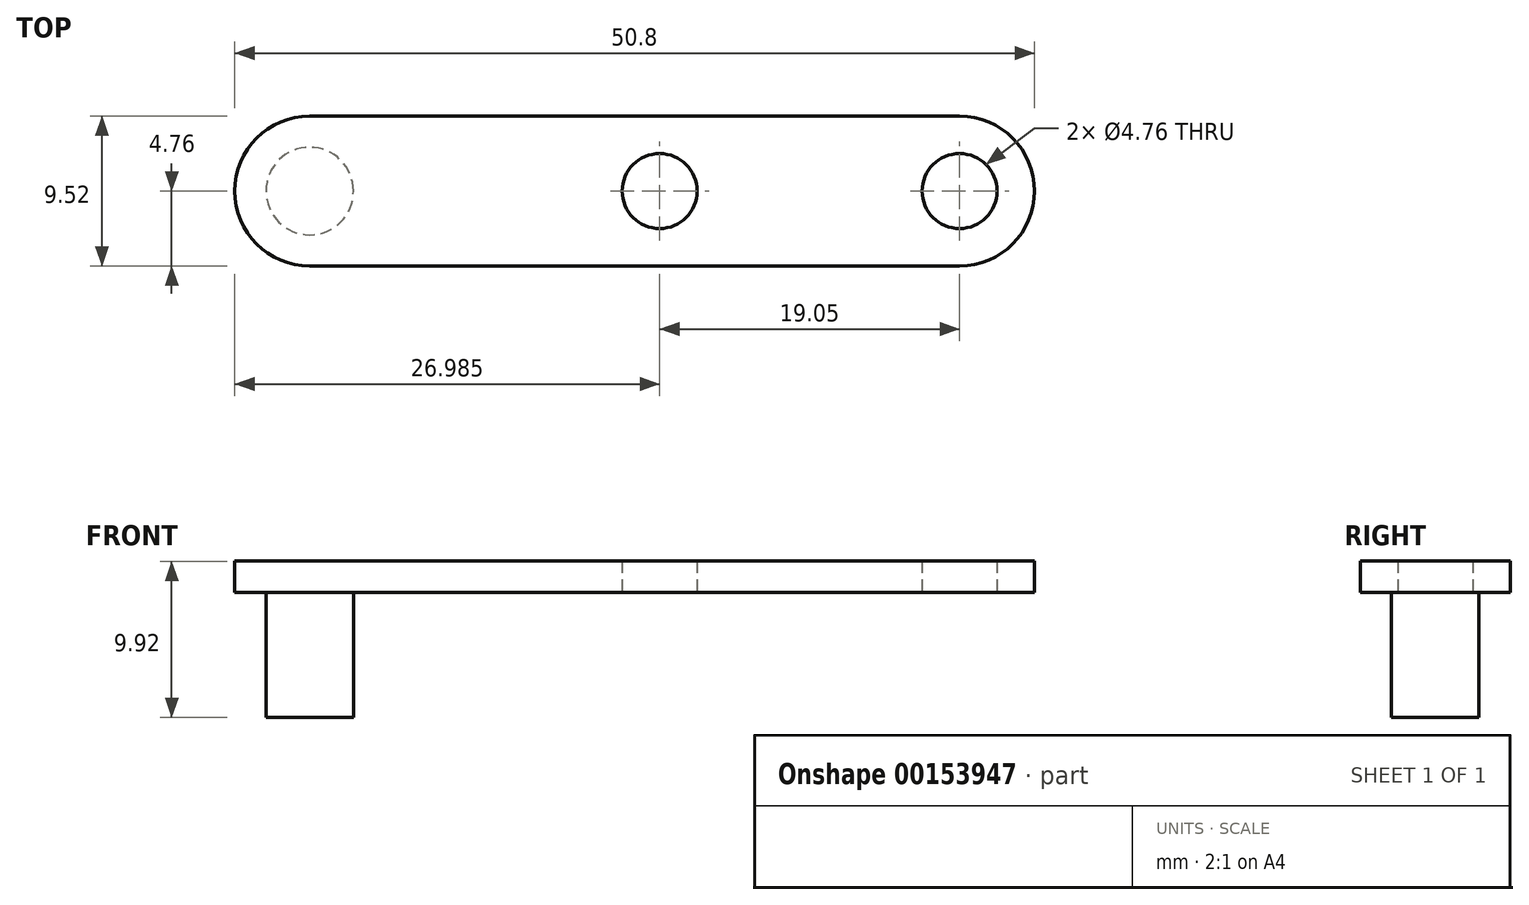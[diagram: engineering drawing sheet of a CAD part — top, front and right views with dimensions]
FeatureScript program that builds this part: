
annotation { "Feature Type Name" : "Feature", "Feature Type Description" : "" }
export const myFeature = defineFeature(function(context is Context, id is Id, definition is map)
    precondition{}
    {
        {
            var Q0;
            Q0=qCreatedBy(makeId("Top.planeOp"),FACE);
            var sketch = newSketch(context, id + "F0", { "sketchPlane" : qUnion([Q0])});
            skArc(sketch, "E0", {"start": v(0, 4.76) * mm, "mid": v(-4.76, 0) * mm, "end": v(0, -4.76) * mm});
            skArc(sketch, "E1", {"start": v(41.27, -4.76) * mm, "mid": v(46.04, 0) * mm, "end": v(41.27, 4.76) * mm});
            skLineSegment(sketch, "E2", {"start": v(0, 4.76) * mm, "end": v(41.27, 4.76) * mm});
            skLineSegment(sketch, "E3", {"start": v(0, -4.76) * mm, "end": v(41.27, -4.76) * mm});
            skPoint(sketch, "E4.orphan", {"position": v(0, -4.76) * mm});
            skCircle(sketch, "E5", {"center": v(0, 0) * mm, "radius": 2.78 * mm});
            skLineSegment(sketch, "E6", {"start": v(22.22, -4.76) * mm, "end": v(22.22, 4.76) * mm, "construction": true});
            skLineSegment(sketch, "E7", {"start": v(41.27, 0) * mm, "end": v(22.22, 0) * mm, "construction": true});
            skSolve(sketch);
        }
        {
            var Q0;
            Q0=makeQuery(id+"F0.imprint","IMPRINT",FACE,{"disambiguationData":[TD([[makeQuery(id+"F0.imprint","IMPRINT",EDGE,{"derivedFrom":sQuery(id+"F0.wireOp",EDGE,"E0")}),1.0]])]});
            var Q1;
            Q1=makeQuery(id+"F0.imprint","IMPRINT",FACE,{"disambiguationData":[TD([[makeQuery(id+"F0.imprint","IMPRINT",EDGE,{"derivedFrom":sQuery(id+"F0.wireOp",EDGE,"E5")}),1.0]])]});
            extrude(context, id + "F1", {"entities" : qUnion([Q0, Q1]), "depth" : 1.98 * mm});
        }
        {
            var Q0;
            Q0=makeQuery(id+"F0.imprint","IMPRINT",FACE,{"disambiguationData":[TD([[makeQuery(id+"F0.imprint","IMPRINT",EDGE,{"derivedFrom":sQuery(id+"F0.wireOp",EDGE,"E5")}),1.0]])]});
            extrude(context, id + "F2", {"entities" : qUnion([Q0]), "operationType" : NewBodyOperationType.ADD, "oppositeDirection" : true, "depth" : 7.94 * mm});
        }
        {
            var Q0;
            Q0=sQuery(id+"F0.wireOp",VERTEX,"E7.end");
            var Q1;
            Q1=sQuery(id+"F0.wireOp",VERTEX,"E1.center");
            var Q2;
            Q2=makeQuery(id+"F1.opExtrude","SWEPT_BODY",BODY,{"disambiguationData":[OSD([sQuery(id+"F0.wireOp",EDGE,"E0"),sQuery(id+"F0.wireOp",EDGE,"E1"),sQuery(id+"F0.wireOp",EDGE,"E2"),sQuery(id+"F0.wireOp",EDGE,"E3")])]});
            hole(context, id + "F3", {"style" : HoleStyle.SIMPLE, "endStyle" : HoleEndStyle.BLIND, "oppositeDirection" : true, "holeDiameter" : 4.76 * mm, "holeDepth" : 12.7 * mm, "locations" : qUnion([Q0, Q1]), "scope" : qUnion([Q2])});
        }
    });
